# Revit family: FU_Sofa_Sandler_Lord Gerrit 221-51
name_source: partatom
category: Furniture
units: mm (PartAtom-declared; Revit-internal decimal feet)

## family parameters
Always vertical = Yes
Cut with Voids When Loaded = No
OmniClass Number = 23.40.20.00
OmniClass Title = General Furniture and Specialties
Room Calculation Point = No
Shared = No
Work Plane-Based = No

## types (1)
- Lord Gerrit 2 221.51
    Default Elevation = 0 mm  [stored 0 ft]
    Depth = 900 mm  [stored 2.95276 ft]
    Description = Fully upholstered 2 seater sofa with solid oak, black walnut or beech frame
    Height = 670 mm  [stored 2.19816 ft]
    Manufacturer = Sandler
    Model = Lord Gerrit 2 221.51
    URL = https://www.sandlerseating.com
    Width = 1600 mm  [stored 5.24934 ft]

note: [stored X ft] marks values corroborated as IEEE doubles in the binary element streams (Revit-internal decimal feet)

## geometry (parser evidence)
native form markers: Sweep x10
no freeform markers — native parametric forms only
